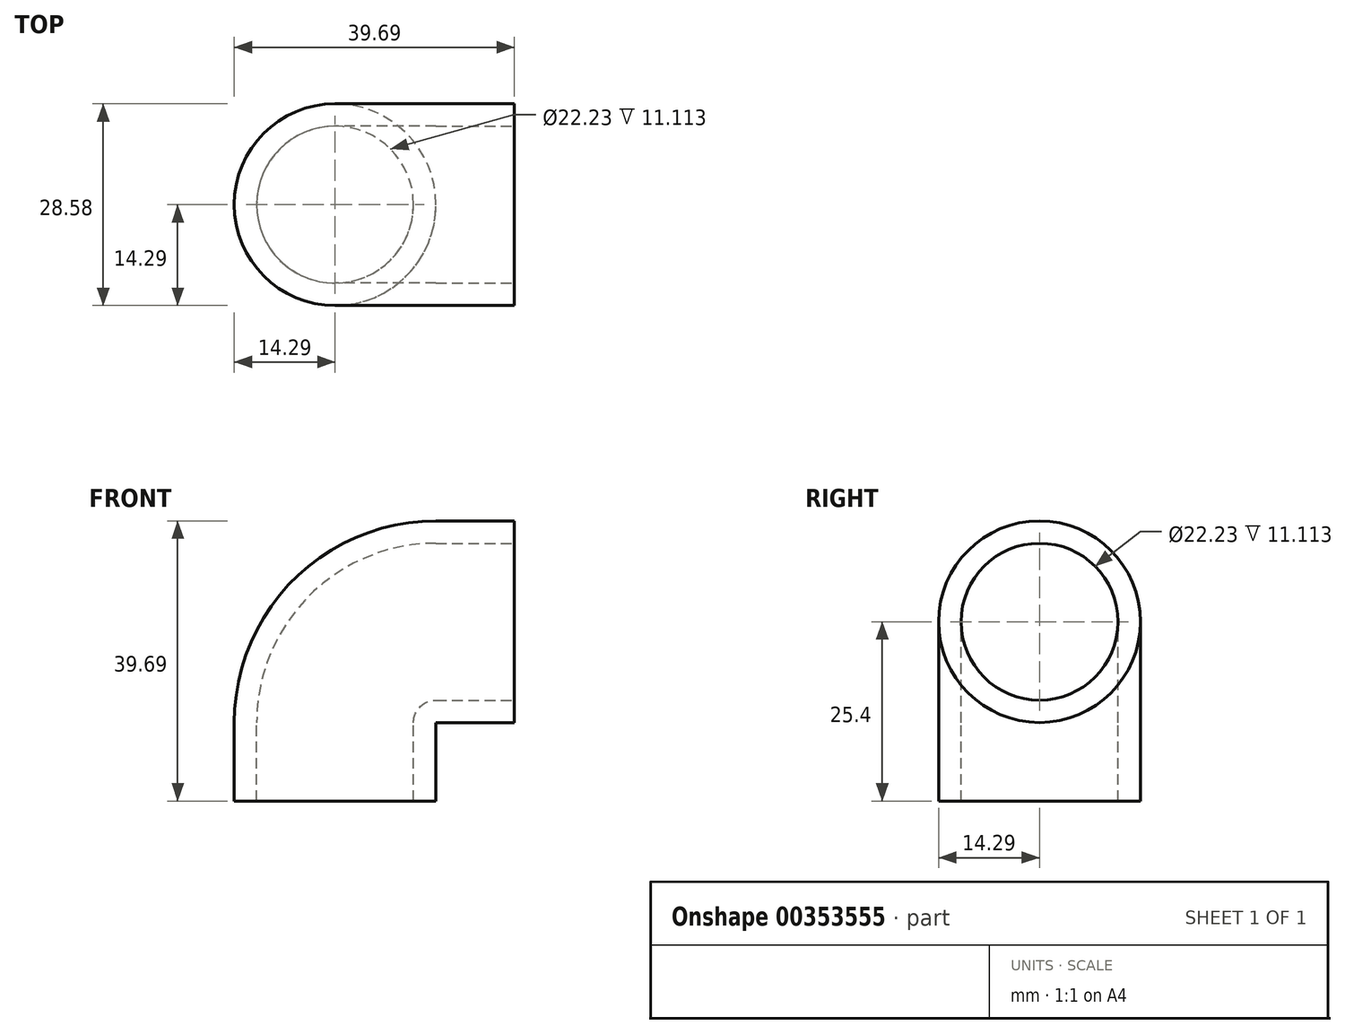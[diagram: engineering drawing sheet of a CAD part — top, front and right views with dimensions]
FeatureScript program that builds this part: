
annotation { "Feature Type Name" : "Feature", "Feature Type Description" : "" }
export const myFeature = defineFeature(function(context is Context, id is Id, definition is map)
    precondition{}
    {
        {
            var Q0;
            Q0=qCreatedBy(makeId("Top.planeOp"),FACE);
            var sketch = newSketch(context, id + "F0", { "sketchPlane" : qUnion([Q0])});
            skCircle(sketch, "E0", {"center": v(0, 0) * mm, "radius": 14.29 * mm});
            skCircle(sketch, "E1", {"center": v(0, 0) * mm, "radius": 11.11 * mm});
            skSolve(sketch);
        }
        {
            var Q0;
            Q0=qCreatedBy(makeId("Front.planeOp"),FACE);
            var sketch = newSketch(context, id + "F1", { "sketchPlane" : qUnion([Q0])});
            skLineSegment(sketch, "E2", {"start": v(0, 0) * mm, "end": v(0, 11.11) * mm});
            skArc(sketch, "E3", {"start": v(14.29, 25.4) * mm, "mid": v(4.18, 21.22) * mm, "end": v(0, 11.11) * mm});
            skLineSegment(sketch, "E4", {"start": v(14.29, 25.4) * mm, "end": v(25.4, 25.4) * mm});
            skSolve(sketch);
        }
        {
            var Q0;
            Q0 = qSketchRegion(id + "F0", true);
            var Q1;
            Q1 = qConstructionFilter(qBodyType(qCreatedBy(id + "F1" ,EDGE), BodyType.WIRE), ConstructionObject.NO);
            sweep(context, id + "F2", {"profiles" : qUnion([Q0]), "path" : qUnion([Q1])});
        }
    });
